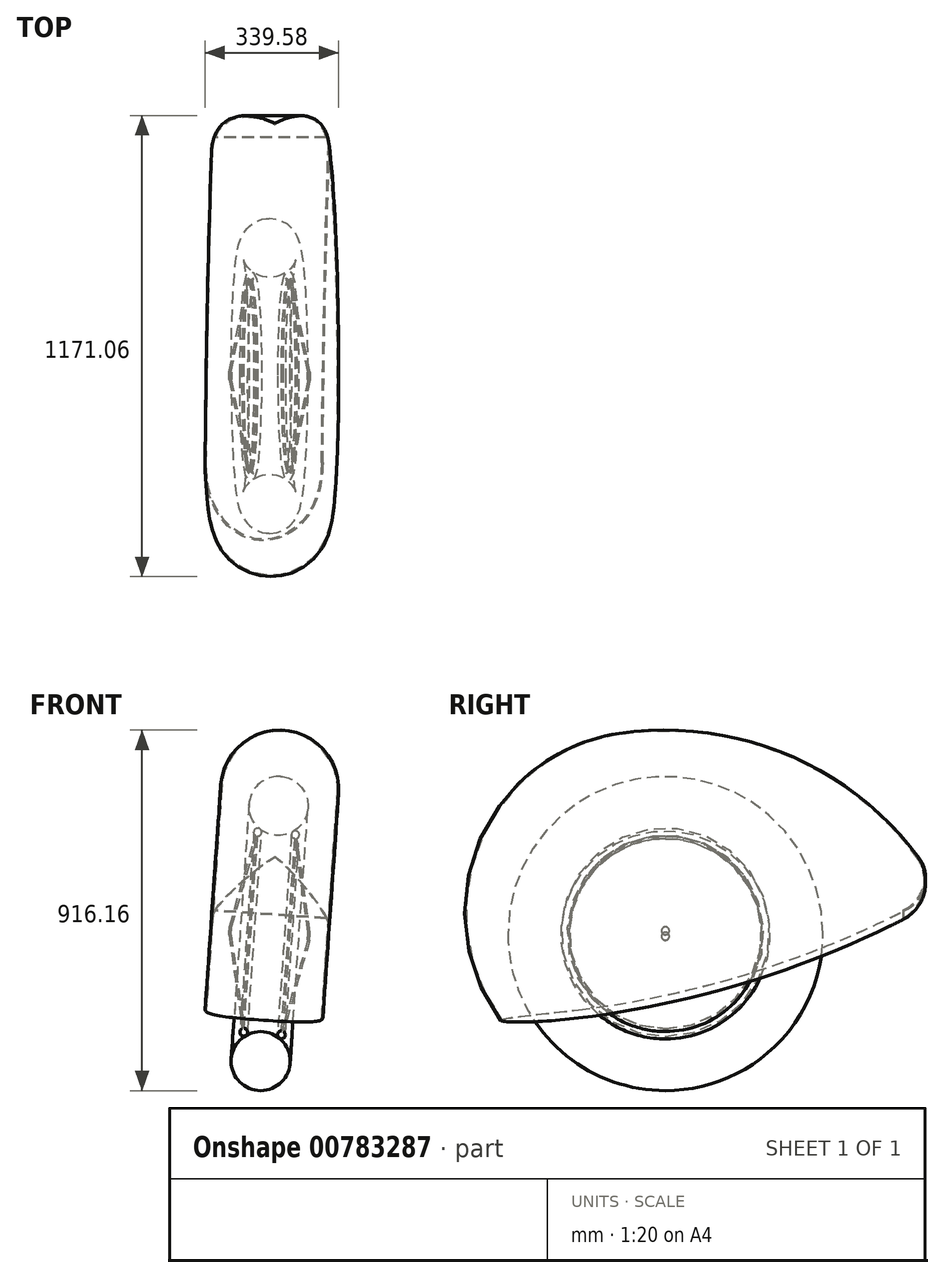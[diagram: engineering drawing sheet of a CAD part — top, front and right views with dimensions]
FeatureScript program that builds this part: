
annotation { "Feature Type Name" : "Feature", "Feature Type Description" : "" }
export const myFeature = defineFeature(function(context is Context, id is Id, definition is map)
    precondition{}
    {
        {
            var Q0;
            Q0=qCreatedBy(makeId("Right.planeOp"),FACE);
            var sketch = newSketch(context, id + "F0", { "sketchPlane" : qUnion([Q0])});
            skLineSegment(sketch, "E0", {"start": v(27, -10.66) * mm, "end": v(41.94, -10.66) * mm});
            skLineSegment(sketch, "E1", {"start": v(1250, 427.7) * mm, "end": v(1250, -634.6) * mm, "construction": true});
            skLineSegment(sketch, "E2", {"start": v(2730, 546.32) * mm, "end": v(2730, -695.58) * mm, "construction": true});
            skLineSegment(sketch, "E3", {"start": v(3850, 768.28) * mm, "end": v(3850, -669.13) * mm});
            skLineSegment(sketch, "E4", {"start": v(270, 349.17) * mm, "end": v(270, -1798.46) * mm, "construction": true});
            skLineSegment(sketch, "E5", {"start": v(0, 219.85) * mm, "end": v(0, -203.28) * mm, "construction": true});
            skLineSegment(sketch, "E6", {"start": v(6030, 178.28) * mm, "end": v(6030, -437.72) * mm, "construction": true});
            skLineSegment(sketch, "E7", {"start": v(270, 349.17) * mm, "end": v(2931.33, 562.45) * mm, "construction": true});
            skArc(sketch, "E8", {"start": v(1302.67, -639.05) * mm, "mid": v(2513.6, -693.52) * mm, "end": v(3725.61, -675.14) * mm, "construction": true});
            skArc(sketch, "E9", {"start": v(0, -203.28) * mm, "mid": v(624.2, -502.3) * mm, "end": v(1302.67, -639.05) * mm, "construction": true});
            skArc(sketch, "E10", {"start": v(6030, 558.28) * mm, "mid": v(4944.43, 709.27) * mm, "end": v(3850, 768.28) * mm});
            skLineSegment(sketch, "E11", {"start": v(3850, 768.28) * mm, "end": v(3182.17, 768.28) * mm, "construction": true});
            skLineSegment(sketch, "E12", {"start": v(0, 8.28) * mm, "end": v(6285.1, 8.28) * mm, "construction": true});
            skLineSegment(sketch, "E13", {"start": v(6285.1, -394.84) * mm, "end": v(6285.1, 178.28) * mm});
            skLineSegment(sketch, "E14", {"start": v(6285.1, 178.28) * mm, "end": v(6030, 178.28) * mm});
            skLineSegment(sketch, "E15", {"start": v(6030, 178.28) * mm, "end": v(6030, 558.28) * mm});
            skLineSegment(sketch, "E16", {"start": v(6030, 178.28) * mm, "end": v(3850, 178.28) * mm, "construction": true});
            skArc(sketch, "E17", {"start": v(3725.61, -675.14) * mm, "mid": v(3789.38, -672.16) * mm, "end": v(3853.14, -668.97) * mm, "construction": true});
            skArc(sketch, "E18", {"start": v(3853.14, -668.97) * mm, "mid": v(5073.28, -568.82) * mm, "end": v(6285.1, -394.84) * mm});
            skLineSegment(sketch, "E19", {"start": v(1305.27, 928.28) * mm, "end": v(2677.63, 928.28) * mm, "construction": true});
            skLineSegment(sketch, "E20", {"start": v(-10, 8.28) * mm, "end": v(-10, -201.72) * mm});
            skArc(sketch, "E21", {"start": v(-344.12, -28.27) * mm, "mid": v(-188.94, -137.87) * mm, "end": v(-10, -201.72) * mm});
            skArc(sketch, "E22", {"start": v(-360, 8.28) * mm, "mid": v(-355.86, -11.64) * mm, "end": v(-344.12, -28.27) * mm});
            skLineSegment(sketch, "E23", {"start": v(-360, 8.28) * mm, "end": v(-10, 8.28) * mm});
            skSolve(sketch);
        }
        {
            var Q0;
            Q0=qCreatedBy(makeId("Front.planeOp"),FACE);
            var Q1;
            Q1=sQuery(id+"F0.wireOp",VERTEX,"E4.start");
            cPlane(context, id + "F1", {"entities" : qUnion([Q0, Q1]), "cplaneType" : CPlaneType.PLANE_POINT, "offset" : 25 * mm, "width" : 150 * mm, "height" : 150 * mm});
        }
        {
            var Q0;
            Q0=qCreatedBy(makeId("Front.planeOp"),FACE);
            var Q1;
            Q1=sQuery(id+"F0.wireOp",VERTEX,"E1.start");
            cPlane(context, id + "F2", {"entities" : qUnion([Q0, Q1]), "cplaneType" : CPlaneType.PLANE_POINT, "offset" : 25 * mm, "width" : 150 * mm, "height" : 150 * mm});
        }
        {
            var Q0;
            Q0=qCreatedBy(makeId("Front.planeOp"),FACE);
            var Q1;
            Q1=sQuery(id+"F0.wireOp",VERTEX,"E2.start");
            cPlane(context, id + "F3", {"entities" : qUnion([Q0, Q1]), "cplaneType" : CPlaneType.PLANE_POINT, "offset" : 25 * mm, "width" : 150 * mm, "height" : 150 * mm});
        }
        {
            var Q0;
            Q0=qCreatedBy(makeId("Front.planeOp"),FACE);
            var Q1;
            Q1=sQuery(id+"F0.wireOp",VERTEX,"E3.start");
            cPlane(context, id + "F4", {"entities" : qUnion([Q0, Q1]), "cplaneType" : CPlaneType.PLANE_POINT, "offset" : 25 * mm, "width" : 150 * mm, "height" : 150 * mm});
        }
        {
            var Q0;
            Q0=qCreatedBy(makeId("Front.planeOp"),FACE);
            var Q1;
            Q1=sQuery(id+"F0.wireOp",VERTEX,"E6.start");
            cPlane(context, id + "F5", {"entities" : qUnion([Q0, Q1]), "cplaneType" : CPlaneType.PLANE_POINT, "offset" : 25 * mm, "width" : 150 * mm, "height" : 150 * mm});
        }
        {
            var Q0;
            Q0=qCreatedBy(makeId("Front.planeOp"),FACE);
            cPlane(context, id + "F6", {"entities" : qUnion([Q0]), "cplaneType" : CPlaneType.OFFSET, "offset" : 1750 * mm, "oppositeDirection" : true, "width" : 150 * mm, "height" : 150 * mm});
        }
        {
            var Q0;
            Q0=qCreatedBy(id+"F6.planeOp",FACE);
            var sketch = newSketch(context, id + "F7", { "sketchPlane" : qUnion([Q0])});
            skCircle(sketch, "E24", {"center": v(952.67, -1375.8) * mm, "radius": 75 * mm});
            skLineSegment(sketch, "E25", {"start": v(1061.16, -1709.17) * mm, "end": v(798.84, -1690.83) * mm, "construction": true});
            skLineSegment(sketch, "E26", {"start": v(952.67, -1375.8) * mm, "end": v(930, -1700) * mm, "construction": true});
            skLineSegment(sketch, "E27", {"start": v(617.06, -1700) * mm, "end": v(930, -1700) * mm, "construction": true});
            skArc(sketch, "E28", {"start": v(999.44, -1458.38) * mm, "mid": v(994.23, -1439.24) * mm, "end": v(994.5, -1459.08) * mm});
            skLineSegment(sketch, "E29", {"start": v(994.5, -1459.08) * mm, "end": v(1027.9, -1696.82) * mm});
            skLineSegment(sketch, "E30", {"start": v(1027.9, -1696.82) * mm, "end": v(1033, -1697.18) * mm});
            skLineSegment(sketch, "E31", {"start": v(1033, -1697.18) * mm, "end": v(999.44, -1458.38) * mm});
            skLineSegment(sketch, "E32", {"start": v(995.62, -1449.14) * mm, "end": v(1030.45, -1697) * mm, "construction": true});
            skSolve(sketch);
        }
        {
            var Q0;
            Q0=makeQuery(id+"F7.imprint","IMPRINT",FACE,{"disambiguationData":[TD([[makeQuery(id+"F7.imprint","IMPRINT",EDGE,{"derivedFrom":sQuery(id+"F7.wireOp",EDGE,"E24")}),1.0]])]});
            var Q1;
            Q1=sQuery(id+"F7.wireOp",EDGE,"E25");
            revolve(context, id + "F8", {"surfaceOperationType" : NewSurfaceOperationType.NEW, "entities" : qUnion([Q0]), "axis" : qUnion([Q1]), "revolveType" : RevolveType.FULL});
        }
        {
            var Q0;
            Q0=sQuery(id+"F7.wireOp",EDGE,"E26");
            cPlane(context, id + "F9", {"entities" : qUnion([Q0]), "cplaneType" : CPlaneType.LINE_ANGLE, "offset" : 930 * mm, "angle" : 180 * degree, "width" : 150 * mm, "height" : 150 * mm});
        }
        {
            var Q0;
            Q0=qCreatedBy(id+"F9.planeOp",FACE);
            var sketch = newSketch(context, id + "F10", { "sketchPlane" : qUnion([Q0])});
            skArc(sketch, "E33", {"start": v(1632.35, -1121.84) * mm, "mid": v(1274.75, -1401.43) * mm, "end": v(1331.25, -1851.83) * mm});
            skArc(sketch, "E34", {"start": v(2453.28, -1531.83) * mm, "mid": v(2107.45, -1197.43) * mm, "end": v(1632.35, -1121.84) * mm});
            skArc(sketch, "E35", {"start": v(1331.25, -1851.83) * mm, "mid": v(1911.2, -1758.2) * mm, "end": v(2453.28, -1531.83) * mm});
            skSolve(sketch);
        }
        {
            var Q0;
            Q0 = qSketchRegion(id + "F10", true);
            extrude(context, id + "F11", {"entities" : qUnion([Q0]), "depth" : 300 * mm, "offsetDistance" : 25 * mm, "symmetric" : true});
        }
        {
            var Q0;
            Q0=makeQuery(id+"F11.opExtrude","SWEPT_EDGE",EDGE,{"disambiguationData":[OSD([sQuery(id+"F10.wireOp",EDGE,"E34"),sQuery(id+"F10.wireOp",EDGE,"E35")])]});
            fillet(context, id + "F12", {"entities" : qUnion([Q0]), "tangentPropagation" : true, "radius" : 100 * mm, "defaultsChanged" : true, "vertexSettings" : [], "allowEdgeOverflow" : false});
        }
        {
            var Q0;
            Q0=makeQuery(id+"F11.opExtrude","CAP_EDGE",EDGE,{"disambiguationData":[OSD([sQuery(id+"F10.wireOp",EDGE,"E33")])],"isStart":false});
            var Q1;
            Q1=makeQuery(id+"F11.opExtrude","CAP_EDGE",EDGE,{"disambiguationData":[OSD([sQuery(id+"F10.wireOp",EDGE,"E34")])],"isStart":false});
            var Q2;
            Q2=makeQuery(id+"F11.opExtrude","CAP_EDGE",EDGE,{"disambiguationData":[OSD([sQuery(id+"F10.wireOp",EDGE,"E33")])],"isStart":true});
            var Q3;
            Q3=makeQuery(id+"F11.opExtrude","CAP_EDGE",EDGE,{"disambiguationData":[OSD([sQuery(id+"F10.wireOp",EDGE,"E34")])],"isStart":true});
            fillet(context, id + "F13", {"entities" : qUnion([Q0, Q1, Q2, Q3]), "radius" : 150 * mm, "defaultsChanged" : false, "vertexSettings" : [], "allowEdgeOverflow" : false});
        }
        {
            var Q0;
            Q0=makeQuery(id+"F11.opExtrude","SWEPT_FACE",FACE,{"disambiguationData":[OSD([sQuery(id+"F10.wireOp",EDGE,"E35")])]});
            shell(context, id + "F14", {"entities" : qUnion([Q0]), "thickness" : 3 * mm});
        }
        {
            var Q0;
            {var subQ0=sQuery(id+"F7.wireOp",EDGE,"E29");Q0=makeQuery(id+"F7.imprint","IMPRINT",FACE,{"disambiguationData":[TD([[makeQuery(id+"F7.imprint","IMPRINT",EDGE,{"derivedFrom":subQ0}),1.0]])]});}
            var Q1;
            Q1=sQuery(id+"F7.wireOp",EDGE,"E25");
            revolve(context, id + "F15", {"surfaceOperationType" : NewSurfaceOperationType.NEW, "entities" : qUnion([Q0]), "axis" : qUnion([Q1]), "revolveType" : RevolveType.FULL});
        }
        {
            var Q0;
            Q0=makeQuery(id+"F15.opRevolve","SWEPT_BODY",BODY,{"disambiguationData":[OSD([sQuery(id+"F7.wireOp",EDGE,"E28"),sQuery(id+"F7.wireOp",EDGE,"E29"),sQuery(id+"F7.wireOp",EDGE,"E30"),sQuery(id+"F7.wireOp",EDGE,"E31")])]});
            var Q1;
            Q1=qCreatedBy(id+"F9.planeOp",FACE);
            mirror(context, id + "F16", {"operationType" : NewBodyOperationType.ADD, "entities" : qUnion([Q0]), "mirrorPlane" : qUnion([Q1])});
        }
    });
